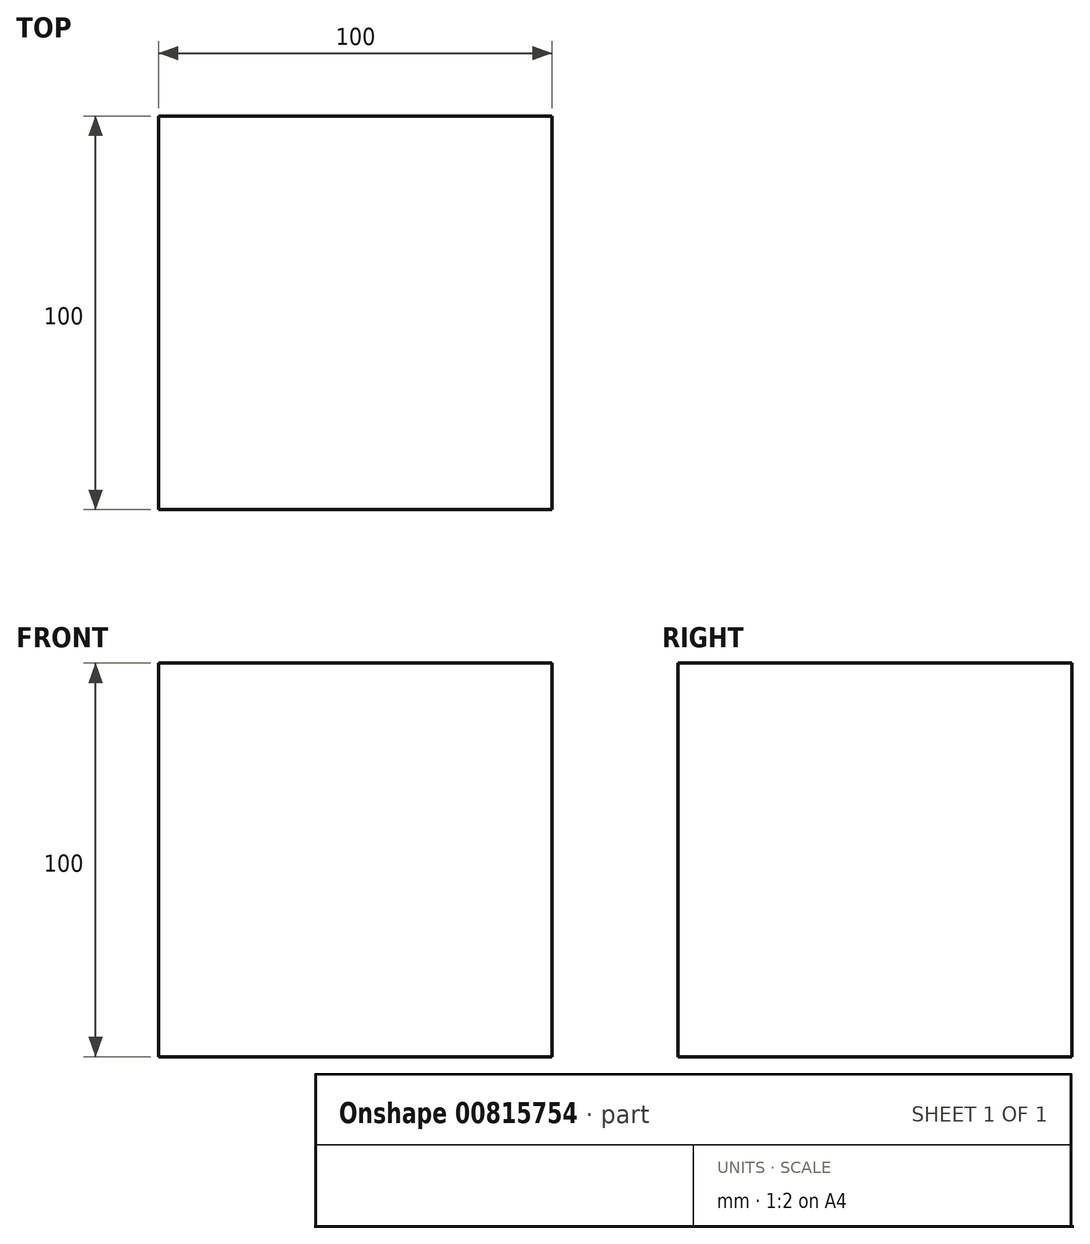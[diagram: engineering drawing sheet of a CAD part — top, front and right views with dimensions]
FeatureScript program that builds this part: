
annotation { "Feature Type Name" : "Feature", "Feature Type Description" : "" }
export const myFeature = defineFeature(function(context is Context, id is Id, definition is map)
    precondition{}
    {
        {
            var Q0;
            Q0=qCreatedBy(makeId("Top.planeOp"),FACE);
            var sketch = newSketch(context, id + "F0", { "sketchPlane" : qUnion([Q0])});
            skLineSegment(sketch, "E0.bottom", {"start": v(50, -50) * mm, "end": v(-50, -50) * mm});
            skLineSegment(sketch, "E0.top", {"start": v(50, 50) * mm, "end": v(-50, 50) * mm});
            skLineSegment(sketch, "E0.left", {"start": v(50, -50) * mm, "end": v(50, 50) * mm});
            skLineSegment(sketch, "E0.right", {"start": v(-50, -50) * mm, "end": v(-50, 50) * mm});
            skPoint(sketch, "E0.middle", {"position": v(0, 0) * mm});
            skSolve(sketch);
        }
        {
            var Q0;
            Q0=makeQuery(id+"F0.imprint","IMPRINT",FACE,{"disambiguationData":[TD([[makeQuery(id+"F0.imprint","IMPRINT",EDGE,{"derivedFrom":sQuery(id+"F0.wireOp",EDGE,"E0.bottom")}),-1.0]])]});
            extrude(context, id + "F1", {"entities" : qUnion([Q0]), "endBound" : BoundingType.SYMMETRIC, "depth" : 100 * mm, "offsetDistance" : 25 * mm});
        }
        {
            var Q0;
            Q0=makeQuery(id+"F1.opExtrude","CAP_VERTEX",VERTEX,{"disambiguationData":[OSD([sQuery(id+"F0.wireOp",EDGE,"E0.top"),sQuery(id+"F0.wireOp",EDGE,"E0.right")])],"isStart":false});
            var Q1;
            Q1=makeQuery(id+"F1.opExtrude","CAP_VERTEX",VERTEX,{"disambiguationData":[OSD([sQuery(id+"F0.wireOp",EDGE,"E0.bottom"),sQuery(id+"F0.wireOp",EDGE,"E0.left")])],"isStart":true});
            var Q2;
            Q2=makeQuery(id+"F1.opExtrude","CAP_VERTEX",VERTEX,{"disambiguationData":[OSD([sQuery(id+"F0.wireOp",EDGE,"E0.bottom"),sQuery(id+"F0.wireOp",EDGE,"E0.right")])],"isStart":true});
            cPlane(context, id + "F2", {"entities" : qUnion([Q0, Q1, Q2]), "cplaneType" : CPlaneType.THREE_POINT, "offset" : 25 * mm, "width" : 150 * mm, "height" : 150 * mm});
        }
        {
            var Q0;
            Q0=qCreatedBy(id+"F2.planeOp",FACE);
            var sketch = newSketch(context, id + "F3", { "sketchPlane" : qUnion([Q0])});
            skLineSegment(sketch, "E1.0", {"start": v(-50, 0) * mm, "end": v(-50, 70.71) * mm});
            skLineSegment(sketch, "E2.0", {"start": v(-50, 0) * mm, "end": v(-50, -70.71) * mm});
            skLineSegment(sketch, "E3.0", {"start": v(50, 70.71) * mm, "end": v(-50, 70.71) * mm});
            skLineSegment(sketch, "E4.0", {"start": v(50, 0) * mm, "end": v(50, 70.71) * mm});
            skLineSegment(sketch, "E5.0", {"start": v(50, 0) * mm, "end": v(50, -70.71) * mm});
            skLineSegment(sketch, "E6.0", {"start": v(50, -70.71) * mm, "end": v(-50, -70.71) * mm});
            skLineSegment(sketch, "E7", {"start": v(-50, 70.71) * mm, "end": v(50, -70.71) * mm});
            skSolve(sketch);
        }
        {
            var Q0;
            Q0=makeQuery(id+"F1.opExtrude","CAP_EDGE",EDGE,{"disambiguationData":[OSD([sQuery(id+"F0.wireOp",EDGE,"E0.right")])],"isStart":false});
            var Q1;
            Q1=makeQuery(id+"F1.opExtrude","SWEPT_EDGE",EDGE,{"disambiguationData":[OSD([sQuery(id+"F0.wireOp",EDGE,"E0.bottom"),sQuery(id+"F0.wireOp",EDGE,"E0.right")])]});
            var Q2;
            Q2=sQuery(id+"F3.wireOp",EDGE,"E6.0");
            var Q3;
            Q3=sQuery(id+"F3.wireOp",EDGE,"E7");
            revolve(context, id + "F4", {"bodyType" : ToolBodyType.SURFACE, "surfaceOperationType" : NewSurfaceOperationType.NEW, "surfaceEntities" : qUnion([Q0, Q1, Q2]), "axis" : qUnion([Q3]), "revolveType" : RevolveType.FULL});
        }
    });
